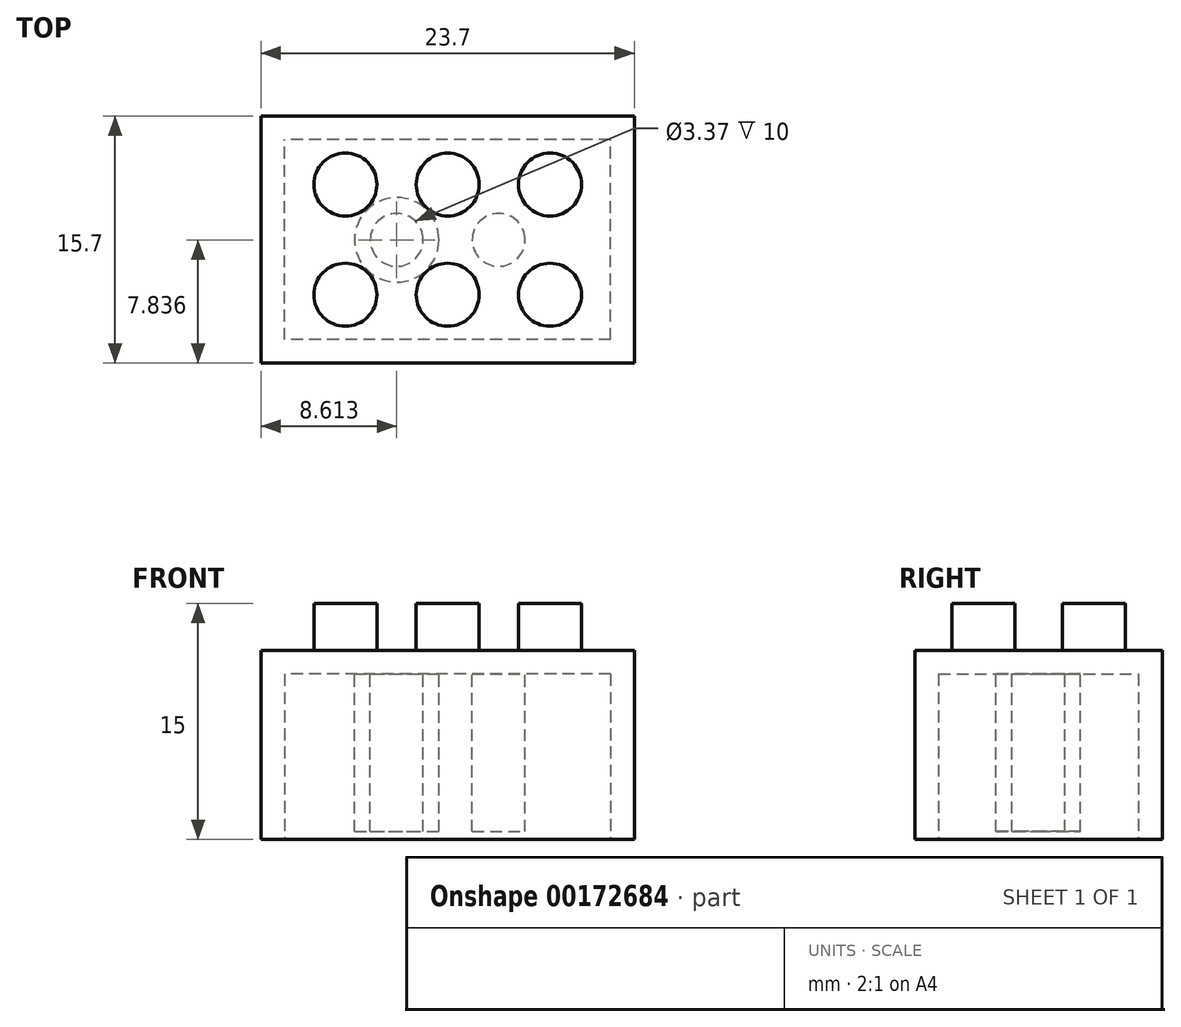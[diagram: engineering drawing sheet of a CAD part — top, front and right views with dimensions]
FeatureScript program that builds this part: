
annotation { "Feature Type Name" : "Feature", "Feature Type Description" : "" }
export const myFeature = defineFeature(function(context is Context, id is Id, definition is map)
    precondition{}
    {
        {
            var Q0;
            Q0=qCreatedBy(makeId("Top.planeOp"),FACE);
            var sketch = newSketch(context, id + "F0", { "sketchPlane" : qUnion([Q0])});
            skLineSegment(sketch, "E0.bottom", {"start": v(0, 0) * mm, "end": v(23.7, 0) * mm});
            skLineSegment(sketch, "E0.top", {"start": v(0, 15.7) * mm, "end": v(23.7, 15.7) * mm});
            skLineSegment(sketch, "E0.left", {"start": v(0, 0) * mm, "end": v(0, 15.7) * mm});
            skLineSegment(sketch, "E0.right", {"start": v(23.7, 0) * mm, "end": v(23.7, 15.7) * mm});
            skSolve(sketch);
        }
        {
            var Q0;
            Q0 = qSketchRegion(id + "F0", true);
            extrude(context, id + "F1", {"entities" : qUnion([Q0]), "depth" : 12 * mm});
        }
        {
            var Q0;
            Q0=makeQuery(id+"F1.opExtrude","CAP_FACE",FACE,{"disambiguationData":[OSD([sQuery(id+"F0.wireOp",EDGE,"E0.bottom"),sQuery(id+"F0.wireOp",EDGE,"E0.top"),sQuery(id+"F0.wireOp",EDGE,"E0.left"),sQuery(id+"F0.wireOp",EDGE,"E0.right")])],"isStart":false});
            var sketch = newSketch(context, id + "F2", { "sketchPlane" : qUnion([Q0])});
            skCircle(sketch, "E1", {"center": v(5.35, 11.35) * mm, "radius": 2 * mm});
            skCircle(sketch, "E2.1.0.0", {"center": v(11.85, 11.35) * mm, "radius": 2 * mm});
            skCircle(sketch, "E2.2.0.0", {"center": v(18.35, 11.35) * mm, "radius": 2 * mm});
            skLineSegment(sketch, "E2.direction1", {"start": v(5.35, 11.35) * mm, "end": v(11.85, 11.35) * mm, "construction": true});
            skLineSegment(sketch, "E3", {"start": v(11.85, 0) * mm, "end": v(11.85, 15.7) * mm, "construction": true});
            skLineSegment(sketch, "E4", {"start": v(0, 7.85) * mm, "end": v(23.7, 7.85) * mm, "construction": true});
            skCircle(sketch, "E5.MirrorC", {"center": v(5.35, 4.35) * mm, "radius": 2 * mm});
            skCircle(sketch, "E6.MirrorC", {"center": v(11.85, 4.35) * mm, "radius": 2 * mm});
            skCircle(sketch, "E7.MirrorC", {"center": v(18.35, 4.35) * mm, "radius": 2 * mm});
            skSolve(sketch);
        }
        {
            var Q0;
            Q0 = qSketchRegion(id + "F2", true);
            extrude(context, id + "F3", {"entities" : qUnion([Q0]), "operationType" : NewBodyOperationType.ADD, "depth" : 3 * mm});
        }
        {
            var Q0;
            Q0=makeQuery(id+"F1.opExtrude","CAP_FACE",FACE,{"disambiguationData":[OSD([sQuery(id+"F0.wireOp",EDGE,"E0.bottom"),sQuery(id+"F0.wireOp",EDGE,"E0.top"),sQuery(id+"F0.wireOp",EDGE,"E0.left"),sQuery(id+"F0.wireOp",EDGE,"E0.right")])],"isStart":true});
            var sketch = newSketch(context, id + "F4", { "sketchPlane" : qUnion([Q0])});
            skLineSegment(sketch, "E8.bottom", {"start": v(22.2, -1.5) * mm, "end": v(1.5, -1.5) * mm});
            skLineSegment(sketch, "E8.top", {"start": v(22.2, -14.2) * mm, "end": v(1.5, -14.2) * mm});
            skLineSegment(sketch, "E8.left", {"start": v(22.2, -1.5) * mm, "end": v(22.2, -14.2) * mm});
            skLineSegment(sketch, "E8.right", {"start": v(1.5, -1.5) * mm, "end": v(1.5, -14.2) * mm});
            skPoint(sketch, "E8.middle", {"position": v(11.85, -7.85) * mm});
            skSolve(sketch);
        }
        {
            var Q0;
            Q0=makeQuery(id+"F4.imprint","IMPRINT",FACE,{"disambiguationData":[TD([[makeQuery(id+"F4.imprint","IMPRINT",EDGE,{"derivedFrom":sQuery(id+"F4.wireOp",EDGE,"E8.bottom")}),1.0]])]});
            extrude(context, id + "F5", {"entities" : qUnion([Q0]), "operationType" : NewBodyOperationType.REMOVE, "oppositeDirection" : true, "depth" : 10.5 * mm});
        }
        {
            var Q0;
            Q0=makeQuery(id+"F5.boolean.opBoolean","COPY",FACE,{"derivedFrom":makeQuery(id+"F5.opExtrude","CAP_FACE",FACE,{"disambiguationData":[OSD([sQuery(id+"F4.wireOp",EDGE,"E8.bottom"),sQuery(id+"F4.wireOp",EDGE,"E8.top"),sQuery(id+"F4.wireOp",EDGE,"E8.left"),sQuery(id+"F4.wireOp",EDGE,"E8.right")])],"isStart":false})});
            var sketch = newSketch(context, id + "F6", { "sketchPlane" : qUnion([Q0])});
            skCircle(sketch, "E9.0.0", {"center": v(5.35, -4.35) * mm, "radius": 2 * mm});
            skCircle(sketch, "E9.1.0", {"center": v(11.85, -4.35) * mm, "radius": 2 * mm});
            skCircle(sketch, "E9.2.0", {"center": v(5.35, -11.35) * mm, "radius": 2 * mm});
            skCircle(sketch, "E9.3.0", {"center": v(11.85, -11.35) * mm, "radius": 2 * mm});
            skCircle(sketch, "E10", {"center": v(8.61, -7.84) * mm, "radius": 2.78 * mm, "construction": true});
            skPoint(sketch, "E10.first.point", {"position": v(6.61, -5.9) * mm});
            skPoint(sketch, "E10.second.point", {"position": v(10.68, -5.97) * mm});
            skPoint(sketch, "E10.third.point", {"position": v(10.42, -9.96) * mm});
            skCircle(sketch, "E11.0", {"center": v(8.61, -7.84) * mm, "radius": 2.68 * mm});
            skCircle(sketch, "E12.0", {"center": v(8.61, -7.84) * mm, "radius": 1.68 * mm});
            skLineSegment(sketch, "E13.0", {"start": v(11.85, 0) * mm, "end": v(11.85, -15.7) * mm, "construction": true});
            skCircle(sketch, "E14.MirrorC", {"center": v(15.09, -7.84) * mm, "radius": 1.68 * mm});
            skCircle(sketch, "E15.MirrorC", {"center": v(15.09, -7.84) * mm, "radius": 2.68 * mm});
            skCircle(sketch, "E16.MirrorC", {"center": v(15.09, -7.84) * mm, "radius": 2.78 * mm, "construction": true});
            skSolve(sketch);
        }
        {
            var Q0;
            Q0=makeQuery(id+"F6.imprint","IMPRINT",FACE,{"disambiguationData":[TD([[makeQuery(id+"F6.imprint","IMPRINT",EDGE,{"derivedFrom":sQuery(id+"F6.wireOp",EDGE,"E11.0")}),1.0]])]});
            var Q1;
            Q1=makeQuery(id+"F6.imprint","IMPRINT",FACE,{"disambiguationData":[TD([[makeQuery(id+"F6.imprint","IMPRINT",EDGE,{"derivedFrom":sQuery(id+"F6.wireOp",EDGE,"E14.MirrorC")}),1.0]])]});
            extrude(context, id + "F7", {"entities" : qUnion([Q0, Q1]), "operationType" : NewBodyOperationType.ADD, "depth" : 10 * mm});
        }
    });
